# Revit family: KR4065551_RegaderaconBrazo_Koral
name_source: partatom
category: Plumbing Fixtures
units: mm (PartAtom-declared; Revit-internal decimal feet)

## family parameters
Always vertical = Yes
Cut with Voids When Loaded = No
Host = Wall
OmniClass Number = 23.31.11.00
OmniClass Title = Faucets
Part Type = Normal
Room Calculation Point = No
Round Connector Dimension = Use Diameter
Shared = No

## types (1)
- Type 1
    Alto = 138 mm  [stored 0.452756 ft]
    Ancho = 152 mm
    Capacidad de flujo = A 80 psi: 9.3 L/min.
    Creado por = BIMBAU
    Default Elevation = 0 mm  [stored 0 ft]
    Description = La regadera Koral con tecnología de ahorro de agua minimiza el derroche ofreciendo un mayor rendimiento sin sacrificar el confort en la ducha, ofrece mayor cobertura para una mayor relajación, ideal par espacios medianos y consumidores que buscan cobertura media. De estilo versátil, se puede combinar en cualquier diseño de baño, cuenta con salidas de agua flexibles que permiten una fácil limpieza y evitan la acumulación de residuos. Con acabado superior, mayor espesor en el cromado, más brillante y resistente a la corrosión.
    Dimensiones generales del producto = 70 x 255 x 255 mm.
    Diámetro abasto = 13 mm
    Fecha de creación = 09/04/2021
    Garantía = 30 años Grival - 5 años Acabados.
    Manufacturer = Corona.
    Material = Corona_Cromado
    Material 2 = Corona_Plastico_Negro
    Material 3 = Corona_Acero inoxidable
    Model = KR4065551_RegaderaconBrazo_Koral
    Peso neto = 520 g. - 1.14 lb.
    Presión máxima recomendada = 125 psi (860 kPa).
    Presión mínima recomendada = 20 psi (140 kPa).
    Profundidad = 329 mm
    Recubrimientos = Resistente a la corrosión, pelado y decoloración por agua. Recubrimientos no tóxicos. Producto para uso doméstico.
    Temperatura de uso = 5° C a 71° C.
    Vida útil = (Junta de bola regadera): 10000 ciclos.

note: [stored X ft] marks values corroborated as IEEE doubles in the binary element streams (Revit-internal decimal feet)

## geometry (parser evidence)
native form markers: Sweep x6
no freeform markers — native parametric forms only
